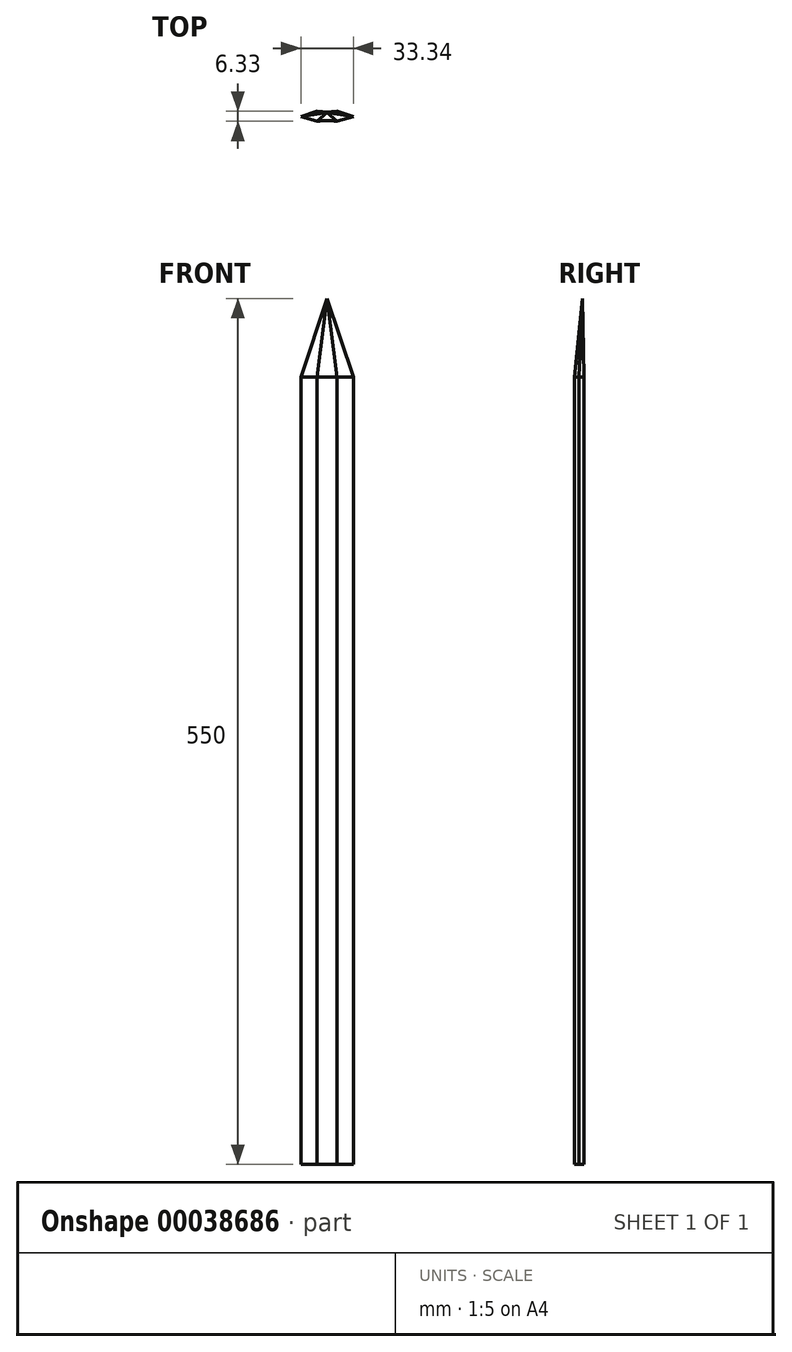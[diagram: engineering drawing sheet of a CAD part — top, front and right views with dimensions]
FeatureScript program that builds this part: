
annotation { "Feature Type Name" : "Feature", "Feature Type Description" : "" }
export const myFeature = defineFeature(function(context is Context, id is Id, definition is map)
    precondition{}
    {
        {
            var Q0;
            Q0=qCreatedBy(makeId("Top.planeOp"),FACE);
            var sketch = newSketch(context, id + "F0", { "sketchPlane" : qUnion([Q0])});
            skLineSegment(sketch, "E0", {"start": v(-16.67, 0) * mm, "end": v(-6.47, 3.36) * mm});
            skLineSegment(sketch, "E1", {"start": v(-16.67, 0) * mm, "end": v(-6.47, -2.97) * mm});
            skArc(sketch, "E2", {"start": v(-6.47, 3.36) * mm, "mid": v(0, 2.9) * mm, "end": v(6.47, 3.36) * mm});
            skArc(sketch, "E3", {"start": v(6.47, -2.97) * mm, "mid": v(0, -2.5) * mm, "end": v(-6.47, -2.97) * mm});
            skLineSegment(sketch, "E4", {"start": v(0, 19.78) * mm, "end": v(0, -22.02) * mm});
            skLineSegment(sketch, "E5.MirrorCS", {"start": v(16.67, 0) * mm, "end": v(6.47, 3.36) * mm});
            skLineSegment(sketch, "E6.MirrorCS", {"start": v(16.67, 0) * mm, "end": v(6.47, -2.97) * mm});
            skSolve(sketch);
        }
        {
            var Q0;
            {var subQ5=sQuery(id+"F0.wireOp",EDGE,"E0");Q0=makeQuery(id+"F0.imprint","IMPRINT",FACE,{"disambiguationData":[TD([[makeQuery(id+"F0.imprint","IMPRINT",EDGE,{"derivedFrom":subQ5}),-1.0]])]});}
            var Q1;
            {var subQ4=sQuery(id+"F0.wireOp",EDGE,"E5.MirrorCS");Q1=makeQuery(id+"F0.imprint","IMPRINT",FACE,{"disambiguationData":[TD([[makeQuery(id+"F0.imprint","IMPRINT",EDGE,{"derivedFrom":subQ4}),1.0]])]});}
            extrude(context, id + "F1", {"entities" : qUnion([Q0, Q1]), "depth" : 500 * mm});
        }
        {
            var Q0;
            Q0=makeQuery(id+"F1.opExtrude","CAP_FACE",FACE,{"disambiguationData":[OSD([sQuery(id+"F0.wireOp",EDGE,"E0"),sQuery(id+"F0.wireOp",EDGE,"E1"),sQuery(id+"F0.wireOp",EDGE,"E2"),sQuery(id+"F0.wireOp",EDGE,"E3"),sQuery(id+"F0.wireOp",EDGE,"E5.MirrorCS"),sQuery(id+"F0.wireOp",EDGE,"E6.MirrorCS")])],"isStart":false});
            var sketch = newSketch(context, id + "F2", { "sketchPlane" : qUnion([Q0])});
            skSolve(sketch);
        }
        {
            var Q0;
            Q0=qCreatedBy(makeId("Top.planeOp"),FACE);
            cPlane(context, id + "F3", {"entities" : qUnion([Q0]), "cplaneType" : CPlaneType.OFFSET, "offset" : 550 * mm, "width" : 150 * mm, "height" : 150 * mm});
        }
        {
            var Q0;
            Q0=qCreatedBy(id+"F3.planeOp",FACE);
            var sketch = newSketch(context, id + "F4", { "sketchPlane" : qUnion([Q0])});
            skPoint(sketch, "E7", {"position": v(0, 2.36) * mm});
            skSolve(sketch);
        }
        {
            var Q1;
            Q1=sQuery(id+"F4.wireOp",VERTEX,"E7");
            var Q2;
            Q2=makeQuery(id+"F2.imprint","IMPRINT",FACE,{"disambiguationData":[TD([[makeQuery(id+"F2.imprint","IMPRINT",EDGE,{"derivedFrom":makeQuery(id+"F1.opExtrude","CAP_EDGE",EDGE,{"disambiguationData":[OSD([sQuery(id+"F0.wireOp",EDGE,"E0")])],"isStart":false})}),-1.0]])]});
            loft(context, id + "F5", {"operationType" : NewBodyOperationType.ADD, "sheetProfilesArray" : [{ "sheetProfileEntities" : qUnion([Q1]) }, { "sheetProfileEntities" : qUnion([Q2]) }]});
        }
    });
